# Revit family: Shower-Showerhead-KOHLER-Katalyst_Air-K-18360A
name_source: partatom
category: Plumbing Fixtures
revit_build: Autodesk Revit 2017 (Build: 20160225_1515(x64)
units: mm (PartAtom-declared; Revit-internal decimal feet)

## family parameters
Cut with Voids When Loaded = No
Host = Face
OmniClass Number = 23.31.17.00
Part Type = Normal
Room Calculation Point = No
Round Connector Dimension = Use Diameter
Shared = No

## types (2) — shared parameters
ADA Compliant = No
Assembly Code = D2010700
CW Connection = No
Cold Water Inlet = Cold Water Inlet
Date Modified = 09/08/2020
Default Elevation = 0"
Description = 8'SQUARE RAINSHOWER HEAD
Drain Included = No
Flow Rate = 3 GPM
HW Connection = Yes
Height = 2 5/8"
Hot Water Inlet = Tempered Water Inlet
Length = 8"
Manufacturer = KOHLER Co.
Master Format 2014 = 22 42 23
Master Format 2014 Name = Residential Showers
Material = Premium Metal Construction
Panel Thickness = 0"
Pressure = 45.00 psi
Product Name = Katalyst
URL = https://www.kohlerasiapacific.com
Vent Connection = No
Waste Connection = No
Waste Water Outlet = Waste Water Outlet
WaterSense Certified = No
Width = 8"

## per-type parameters (varying)
| type | Finish | Model | Type |
| CP-Polished Chrome | Kohler-Metal-CP-Polished_Chrome | K-18360A-CP | 1 |
| 2BL-Original Black | Kohler-Metal-2BL-Original_Black | K-18360A-2BL | 2 |

## geometry (parser evidence)
native form markers: Sweep x5
no freeform markers — native parametric forms only
